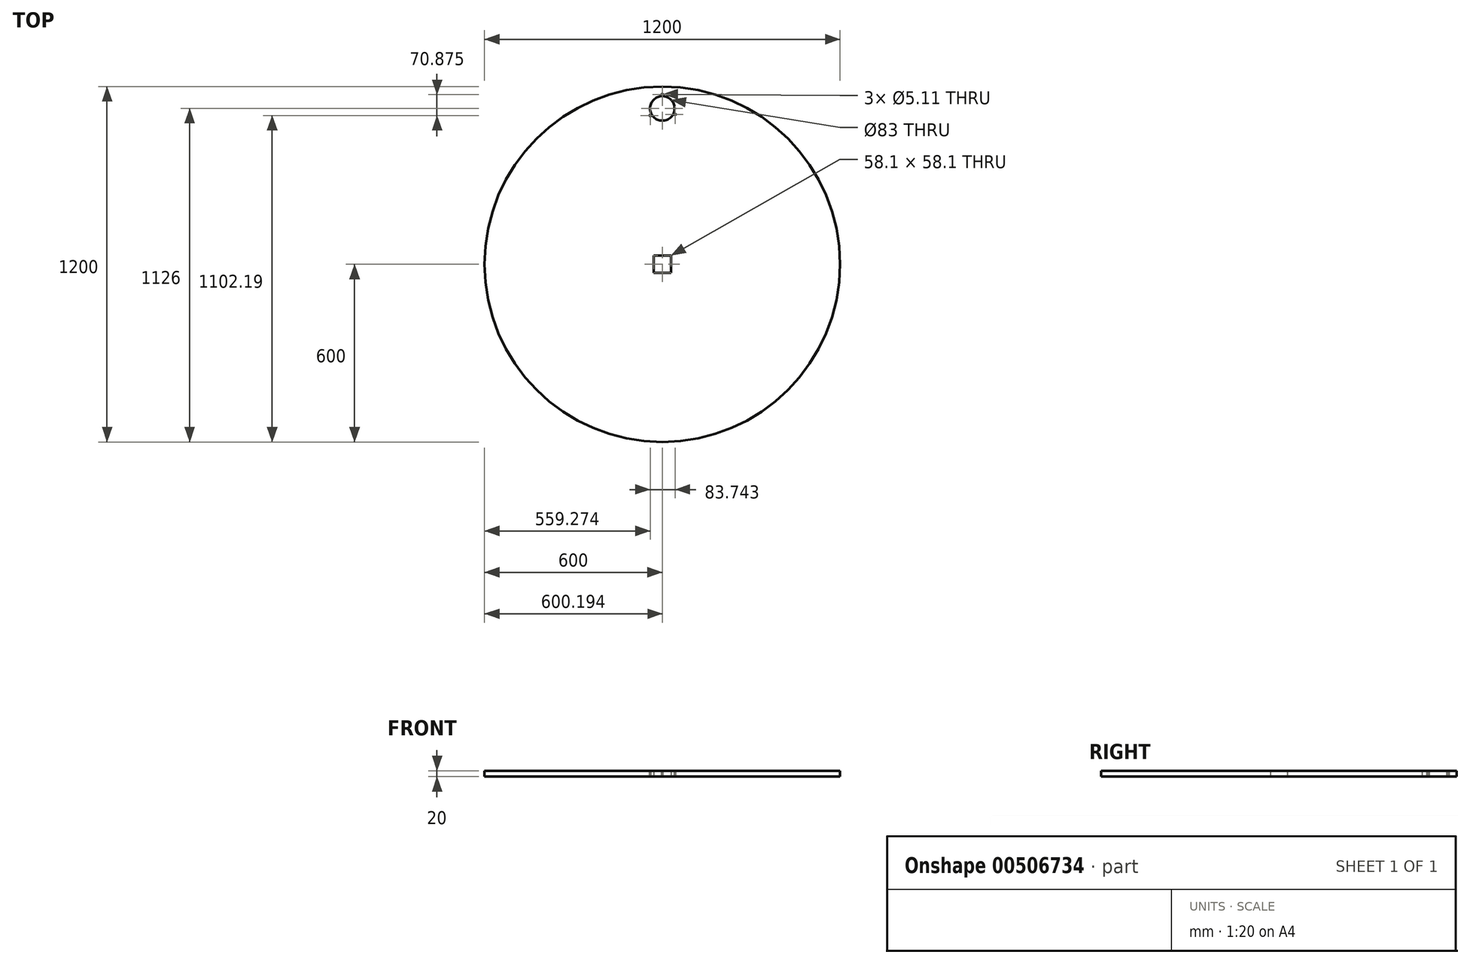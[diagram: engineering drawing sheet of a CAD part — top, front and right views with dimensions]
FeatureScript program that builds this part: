
annotation { "Feature Type Name" : "Feature", "Feature Type Description" : "" }
export const myFeature = defineFeature(function(context is Context, id is Id, definition is map)
    precondition{}
    {
        {
            var Q0;
            Q0=qCreatedBy(makeId("Top.planeOp"),FACE);
            var sketch = newSketch(context, id + "F0", { "sketchPlane" : qUnion([Q0])});
            skCircle(sketch, "E0", {"center": v(0, 0) * mm, "radius": 600 * mm});
            skLineSegment(sketch, "E1.bottom", {"start": v(29.05, 29.05) * mm, "end": v(-29.05, 29.05) * mm});
            skLineSegment(sketch, "E1.top", {"start": v(29.05, -29.05) * mm, "end": v(-29.05, -29.05) * mm});
            skLineSegment(sketch, "E1.left", {"start": v(29.05, 29.05) * mm, "end": v(29.05, -29.05) * mm});
            skLineSegment(sketch, "E1.right", {"start": v(-29.05, 29.05) * mm, "end": v(-29.05, -29.05) * mm});
            skLineSegment(sketch, "E2.bottom", {"start": v(37.05, 37.05) * mm, "end": v(-37.05, 37.05) * mm, "construction": true});
            skLineSegment(sketch, "E2.top", {"start": v(37.05, -37.05) * mm, "end": v(-37.05, -37.05) * mm, "construction": true});
            skLineSegment(sketch, "E2.left", {"start": v(37.05, 37.05) * mm, "end": v(37.05, -37.05) * mm, "construction": true});
            skLineSegment(sketch, "E2.right", {"start": v(-37.05, 37.05) * mm, "end": v(-37.05, -37.05) * mm, "construction": true});
            skSolve(sketch);
        }
        {
            var Q0;
            Q0 = qSketchRegion(id + "F0", true);
            extrude(context, id + "F1", {"entities" : qUnion([Q0]), "depth" : 20 * mm, "offsetDistance" : 25 * mm});
        }
        {
            var Q0;
            Q0=makeQuery(id+"F1.opExtrude","CAP_FACE",FACE,{"disambiguationData":[OSD([sQuery(id+"F0.wireOp",EDGE,"E0"),sQuery(id+"F0.wireOp",EDGE,"E1.bottom"),sQuery(id+"F0.wireOp",EDGE,"E1.top"),sQuery(id+"F0.wireOp",EDGE,"E1.left"),sQuery(id+"F0.wireOp",EDGE,"E1.right"),sQuery(id+"F0.wireOp",EDGE,"073765de-ee5e-4c73-8d72-9c4c39485c3f")])],"isStart":false});
            cPlane(context, id + "F2", {"entities" : qUnion([Q0]), "cplaneType" : CPlaneType.OFFSET, "offset" : 0 * mm, "width" : 150 * mm, "height" : 150 * mm});
        }
        {
            var Q0;
            Q0=qCreatedBy(id+"F2.planeOp",FACE);
            var sketch = newSketch(context, id + "F3", { "sketchPlane" : qUnion([Q0])});
            skCircle(sketch, "E3.0", {"center": v(0.2, 526) * mm, "radius": 41.5 * mm});
            skCircle(sketch, "E4.0", {"center": v(0.2, 573.07) * mm, "radius": 2.2 * mm, "construction": true});
            skLineSegment(sketch, "E5.0", {"start": v(0.2, 576.82) * mm, "end": v(0.2, 569.32) * mm, "construction": true});
            skCircle(sketch, "E6.0", {"center": v(43.02, 505.85) * mm, "radius": 2.2 * mm, "construction": true});
            skLineSegment(sketch, "E6.1", {"start": v(0.2, 525.82) * mm, "end": v(46.42, 504.26) * mm, "construction": true});
            skLineSegment(sketch, "E7.0", {"start": v(0.2, 525.82) * mm, "end": v(-43.97, 500.32) * mm, "construction": true});
            skCircle(sketch, "E7.1", {"center": v(-40.73, 502.2) * mm, "radius": 2.2 * mm, "construction": true});
            skLineSegment(sketch, "E8", {"start": v(0, 0) * mm, "end": v(0.2, 526) * mm, "construction": true});
            skSolve(sketch);
        }
        {
            var Q0;
            Q0=makeQuery(id+"F3.imprint","IMPRINT",FACE,{"disambiguationData":[TD([[makeQuery(id+"F3.imprint","IMPRINT",EDGE,{"derivedFrom":sQuery(id+"F3.wireOp",EDGE,"E3.0")}),1.0]])]});
            extrude(context, id + "F4", {"entities" : qUnion([Q0]), "operationType" : NewBodyOperationType.REMOVE, "endBound" : BoundingType.THROUGH_ALL, "oppositeDirection" : true, "depth" : 25 * mm, "offsetDistance" : 25 * mm});
        }
        {
            var Q0;
            Q0=sQuery(id+"F3.wireOp",VERTEX,"E7.1.center");
            var Q1;
            Q1=sQuery(id+"F3.wireOp",VERTEX,"E6.0.center");
            var Q2;
            Q2=sQuery(id+"F3.wireOp",VERTEX,"E4.0.center");
            var Q3;
            Q3=makeQuery(id+"F1.opExtrude","SWEPT_BODY",BODY,{"disambiguationData":[OSD([sQuery(id+"F0.wireOp",EDGE,"E0"),sQuery(id+"F0.wireOp",EDGE,"E1.bottom"),sQuery(id+"F0.wireOp",EDGE,"E1.top"),sQuery(id+"F0.wireOp",EDGE,"E1.left"),sQuery(id+"F0.wireOp",EDGE,"E1.right")])]});
            hole(context, id + "F5", {"style" : HoleStyle.SIMPLE, "endStyle" : HoleEndStyle.BLIND, "standardTappedOrClearance" : lookupTablePath({ "standard" : "ANSI", "engagement" : "75%", "pitch" : "20 tpi", "size" : "1/4", "type" : "Tapped" }), "standardBlindInLast" : lookupTablePath({ "standard" : "ANSI", "engagement" : "75%", "pitch" : "20 tpi", "size" : "1/4", "type" : "Tapped" }), "holeDiameter" : 5.1 * mm, "majorDiameter" : 6.35 * mm, "showTappedDepth" : true, "holeDepth" : 15.8 * mm, "tappedDepth" : 12 * mm, "tapClearance" : 3, "locations" : qUnion([Q0, Q1, Q2]), "scope" : qUnion([Q3])});
        }
    });
